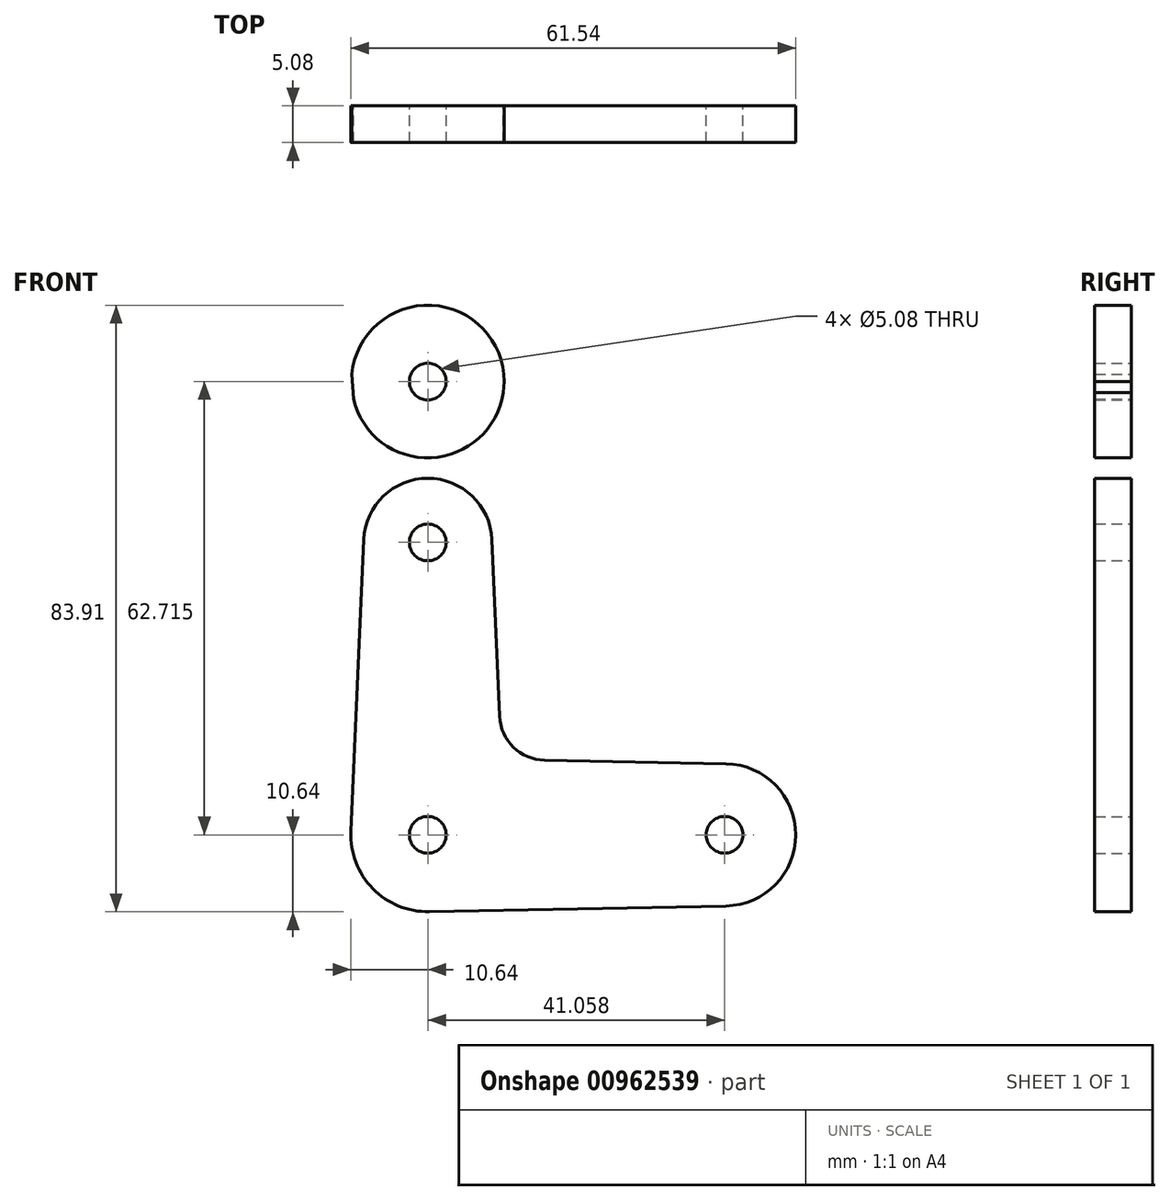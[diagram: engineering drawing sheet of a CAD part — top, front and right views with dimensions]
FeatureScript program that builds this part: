
annotation { "Feature Type Name" : "Feature", "Feature Type Description" : "" }
export const myFeature = defineFeature(function(context is Context, id is Id, definition is map)
    precondition{}
    {
        {
            var Q0;
            Q0=qCreatedBy(makeId("Front.planeOp"),FACE);
            var sketch = newSketch(context, id + "F0", { "sketchPlane" : qUnion([Q0])});
            skCircle(sketch, "E0", {"center": v(0, 0) * mm, "radius": 10.64 * mm});
            skCircle(sketch, "E1", {"center": v(41.06, 0) * mm, "radius": 9.84 * mm});
            skCircle(sketch, "E2", {"center": v(0, 62.71) * mm, "radius": 10.55 * mm});
            skCircle(sketch, "E3", {"center": v(0, 40.46) * mm, "radius": 8.88 * mm});
            skLineSegment(sketch, "E4", {"start": v(0, 62.71) * mm, "end": v(0, 0) * mm, "construction": true});
            skLineSegment(sketch, "E5", {"start": v(41.06, 0) * mm, "end": v(0, 0) * mm, "construction": true});
            skLineSegment(sketch, "E6", {"start": v(-10.5, 63.71) * mm, "end": v(-8.86, 39.84) * mm});
            skLineSegment(sketch, "E7", {"start": v(10.55, 62.7) * mm, "end": v(8.85, 39.8) * mm});
            skLineSegment(sketch, "E8", {"start": v(-8.87, 40.84) * mm, "end": v(-10.63, 0.46) * mm});
            skLineSegment(sketch, "E9", {"start": v(8.87, 40.84) * mm, "end": v(9.93, 16.4) * mm});
            skLineSegment(sketch, "E10", {"start": v(0.2, -10.63) * mm, "end": v(41.25, -9.84) * mm});
            skLineSegment(sketch, "E11", {"start": v(16.15, 10.33) * mm, "end": v(41.25, 9.84) * mm});
            skCircle(sketch, "E12", {"center": v(0, 0) * mm, "radius": 2.54 * mm});
            skCircle(sketch, "E13", {"center": v(0, 40.46) * mm, "radius": 2.54 * mm});
            skCircle(sketch, "E14", {"center": v(41.06, 0) * mm, "radius": 2.54 * mm});
            skCircle(sketch, "E15", {"center": v(0, 62.71) * mm, "radius": 2.54 * mm});
            skArc(sketch, "E16.filletArc", {"start": v(9.93, 16.4) * mm, "mid": v(11.84, 12.13) * mm, "end": v(16.15, 10.33) * mm});
            skSolve(sketch);
        }
        {
            var Q0;
            Q0=makeQuery(id+"F0.imprint","IMPRINT",FACE,{"disambiguationData":[TD([[makeQuery(id+"F0.imprint","IMPRINT",EDGE,{"derivedFrom":sQuery(id+"F0.wireOp",EDGE,"E13")}),-1.0]])]});
            var Q1;
            Q1=makeQuery(id+"F0.imprint","IMPRINT",FACE,{"disambiguationData":[TD([[makeQuery(id+"F0.imprint","IMPRINT",EDGE,{"derivedFrom":sQuery(id+"F0.wireOp",EDGE,"E14")}),-1.0]])]});
            var Q2;
            {var subQ10=sQuery(id+"F0.wireOp",EDGE,"E10");Q2=makeQuery(id+"F0.imprint","IMPRINT",FACE,{"disambiguationData":[TD([[makeQuery(id+"F0.imprint","IMPRINT",EDGE,{"derivedFrom":subQ10}),1.0]])]});}
            var Q3;
            Q3=makeQuery(id+"F0.imprint","IMPRINT",FACE,{"disambiguationData":[TD([[makeQuery(id+"F0.imprint","IMPRINT",EDGE,{"derivedFrom":sQuery(id+"F0.wireOp",EDGE,"E15")}),-1.0]])]});
            var Q4;
            Q4=makeQuery(id+"F0.imprint","IMPRINT",FACE,{"disambiguationData":[TD([[makeQuery(id+"F0.imprint","IMPRINT",EDGE,{"derivedFrom":sQuery(id+"F0.wireOp",EDGE,"E12")}),-1.0]])]});
            var Q5;
            {var subQ1=sQuery(id+"F0.wireOp",EDGE,"E2");var subQ5=sQuery(id+"F0.wireOp",EDGE,"E6");var subQ6=makeQuery(id+"F0.imprint","INTERSECT",VERTEX,{"disambiguationData":[OD(1.0)],"derivedFrom":[subQ1,subQ5]});Q5=makeQuery(id+"F0.imprint","IMPRINT",FACE,{"disambiguationData":[TD([[makeQuery(id+"F0.imprint","IMPRINT",EDGE,{"disambiguationData":[TD([[subQ6,-1.0]])],"derivedFrom":subQ1}),-1.0]])]});}
            var Q6;
            {var subQ0=sQuery(id+"F0.wireOp",EDGE,"E6");var subQ1=sQuery(id+"F0.wireOp",EDGE,"E2");var subQ2=makeQuery(id+"F0.imprint","INTERSECT",VERTEX,{"disambiguationData":[OD(0.0)],"derivedFrom":[subQ1,subQ0]});Q6=makeQuery(id+"F0.imprint","IMPRINT",FACE,{"disambiguationData":[TD([[makeQuery(id+"F0.imprint","IMPRINT",EDGE,{"disambiguationData":[TD([[subQ2,-1.0]])],"derivedFrom":subQ1}),1.0]])]});}
            var Q7;
            {var subQ0=sQuery(id+"F0.wireOp",EDGE,"E7");var subQ1=sQuery(id+"F0.wireOp",EDGE,"E3");var subQ2=makeQuery(id+"F0.imprint","INTERSECT",VERTEX,{"derivedFrom":[subQ1,subQ0]});Q7=makeQuery(id+"F0.imprint","IMPRINT",FACE,{"disambiguationData":[TD([[makeQuery(id+"F0.imprint","IMPRINT",EDGE,{"disambiguationData":[TD([[subQ2,-1.0]])],"derivedFrom":subQ1}),-1.0]])]});}
            var Q8;
            {var subQ0=sQuery(id+"F0.wireOp",EDGE,"E7");var subQ1=sQuery(id+"F0.wireOp",EDGE,"E2");var subQ2=makeQuery(id+"F0.imprint","INTERSECT",VERTEX,{"disambiguationData":[OD(0.0)],"derivedFrom":[subQ1,subQ0]});Q8=makeQuery(id+"F0.imprint","IMPRINT",FACE,{"disambiguationData":[TD([[makeQuery(id+"F0.imprint","IMPRINT",EDGE,{"disambiguationData":[TD([[subQ2,1.0]])],"derivedFrom":subQ1}),1.0]])]});}
            var Q9;
            {var subQ0=sQuery(id+"F0.wireOp",EDGE,"E6");var subQ1=sQuery(id+"F0.wireOp",EDGE,"E3");var subQ2=makeQuery(id+"F0.imprint","INTERSECT",VERTEX,{"derivedFrom":[subQ1,subQ0]});Q9=makeQuery(id+"F0.imprint","IMPRINT",FACE,{"disambiguationData":[TD([[makeQuery(id+"F0.imprint","IMPRINT",EDGE,{"disambiguationData":[TD([[subQ2,1.0]])],"derivedFrom":subQ1}),-1.0]])]});}
            extrude(context, id + "F1", {"entities" : qUnion([Q0, Q1, Q2, Q3, Q4, Q5, Q6, Q7, Q8, Q9]), "depth" : 5.08 * mm, "offsetDistance" : 25.4 * mm});
        }
    });
